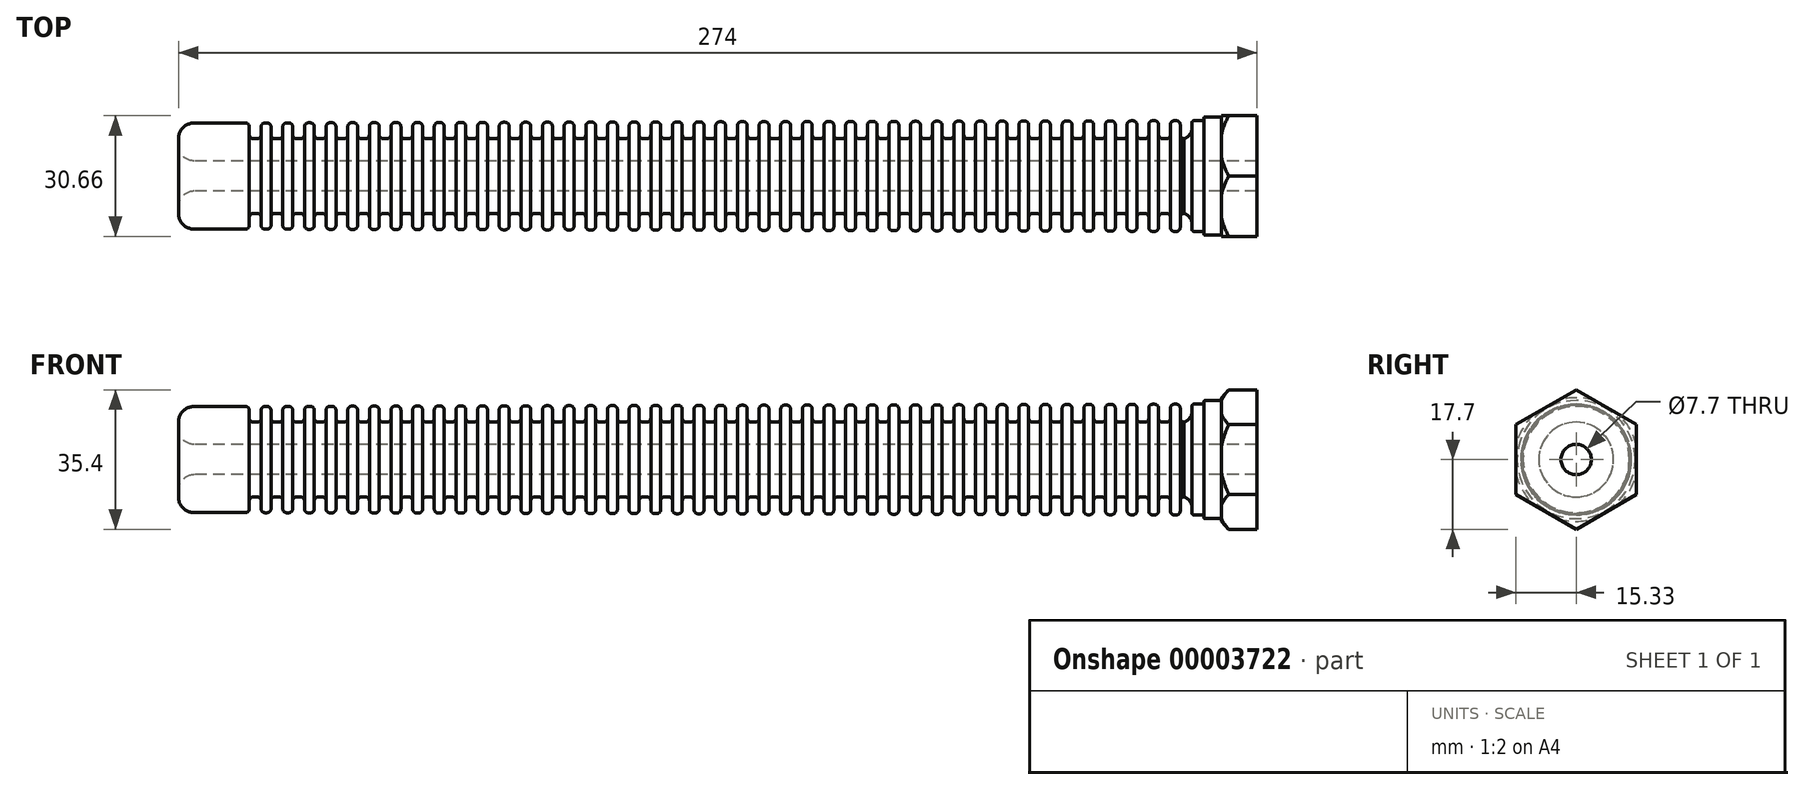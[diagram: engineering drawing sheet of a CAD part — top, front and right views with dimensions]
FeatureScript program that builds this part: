
annotation { "Feature Type Name" : "Feature", "Feature Type Description" : "" }
export const myFeature = defineFeature(function(context is Context, id is Id, definition is map)
    precondition{}
    {
        {
            var Q0;
            Q0=qCreatedBy(makeId("Front.planeOp"),FACE);
            var sketch = newSketch(context, id + "F0", { "sketchPlane" : qUnion([Q0])});
            skLineSegment(sketch, "E0", {"start": v(-577.5, 0) * mm, "end": v(0, 0) * mm, "construction": true});
            skLineSegment(sketch, "E1.0.MirrorCS", {"start": v(577.5, 0) * mm, "end": v(0, 0) * mm, "construction": true});
            skLineSegment(sketch, "E2", {"start": v(-577.5, 0) * mm, "end": v(-577.5, 13.5) * mm, "construction": true});
            skLineSegment(sketch, "E3.0.MirrorCS", {"start": v(-577.5, 0) * mm, "end": v(-577.5, -13.5) * mm, "construction": true});
            skLineSegment(sketch, "E4", {"start": v(-577.5, 13.5) * mm, "end": v(-577.5, 3.85) * mm});
            skLineSegment(sketch, "E5.0.MirrorCS", {"start": v(-577.5, -13.5) * mm, "end": v(-577.5, -3.85) * mm});
            skLineSegment(sketch, "E6", {"start": v(-577.5, 3.85) * mm, "end": v(-559.5, 3.85) * mm});
            skLineSegment(sketch, "E7", {"start": v(-577.5, 13.5) * mm, "end": v(-559.5, 13.5) * mm});
            skLineSegment(sketch, "E8.0.MirrorCS", {"start": v(-577.5, -13.5) * mm, "end": v(-559.5, -13.5) * mm});
            skLineSegment(sketch, "E9.0.MirrorCS", {"start": v(-577.5, -3.85) * mm, "end": v(56.5, -3.85) * mm});
            skLineSegment(sketch, "E10", {"start": v(-559.5, 13.5) * mm, "end": v(-559.5, 3.85) * mm});
            skPoint(sketch, "E11", {"position": v(-577.5, 15) * mm});
            skPoint(sketch, "E12.0.MirrorP", {"position": v(-577.5, -15) * mm});
            skLineSegment(sketch, "E13", {"start": v(-577.5, 15) * mm, "end": v(56.5, 15) * mm, "construction": true});
            skLineSegment(sketch, "E14", {"start": v(-559.5, 9.5) * mm, "end": v(-559.5, 9.5) * mm});
            skPoint(sketch, "E15.trimOffspring.end.orphan", {"position": v(56.5, 3.85) * mm});
            skLineSegment(sketch, "E16", {"start": v(-559.5, 3.85) * mm, "end": v(56.5, 3.85) * mm});
            skPoint(sketch, "E17.end.orphan", {"position": v(-559.5, 13.5) * mm});
            skLineSegment(sketch, "E18", {"start": v(-559.5, 13.5) * mm, "end": v(-559.5, 13.5) * mm});
            skLineSegment(sketch, "E19", {"start": v(-559.5, 13.5) * mm, "end": v(56.5, 15) * mm, "construction": true});
            skLineSegment(sketch, "E20", {"start": v(-559.5, 9.5) * mm, "end": v(56.5, 9.5) * mm});
            skLineSegment(sketch, "E21", {"start": v(-559.5, 13.5) * mm, "end": v(56.5, 13.5) * mm, "construction": true});
            skLineSegment(sketch, "E22", {"start": v(-556.5, 13.5) * mm, "end": v(-556.5, 9.5) * mm});
            skLineSegment(sketch, "E23", {"start": v(-556.5, 13.5) * mm, "end": v(-554, 13.5) * mm});
            skLineSegment(sketch, "E24", {"start": v(-554, 13.5) * mm, "end": v(-554, 9.5) * mm});
            skLineSegment(sketch, "E25", {"start": v(-551, 13.52) * mm, "end": v(-551, 13.5) * mm});
            skLineSegment(sketch, "E26", {"start": v(-551, 13.52) * mm, "end": v(-548.5, 13.52) * mm});
            skLineSegment(sketch, "E27", {"start": v(-548.5, 13.52) * mm, "end": v(-548.5, 9.5) * mm});
            skPoint(sketch, "E28", {"position": v(-312.5, 3.85) * mm});
            skLineSegment(sketch, "E29", {"start": v(-545.5, 13.53) * mm, "end": v(-545.5, 9.5) * mm});
            skLineSegment(sketch, "E30", {"start": v(-545.5, 13.53) * mm, "end": v(-543, 13.53) * mm});
            skLineSegment(sketch, "E31", {"start": v(-543, 13.53) * mm, "end": v(-543, 9.5) * mm});
            skLineSegment(sketch, "E32", {"start": v(-540, 13.55) * mm, "end": v(-540, 9.5) * mm});
            skLineSegment(sketch, "E33", {"start": v(-540, 13.55) * mm, "end": v(-537.5, 13.55) * mm});
            skLineSegment(sketch, "E34", {"start": v(-537.5, 13.55) * mm, "end": v(-537.5, 9.5) * mm});
            skLineSegment(sketch, "E35", {"start": v(-534.5, 13.56) * mm, "end": v(-534.5, 9.5) * mm});
            skLineSegment(sketch, "E36", {"start": v(-534.5, 13.56) * mm, "end": v(-532, 13.56) * mm});
            skLineSegment(sketch, "E37", {"start": v(-532, 13.56) * mm, "end": v(-532, 9.5) * mm});
            skLineSegment(sketch, "E38", {"start": v(-529, 13.57) * mm, "end": v(-529, 9.5) * mm});
            skLineSegment(sketch, "E39", {"start": v(-529, 13.57) * mm, "end": v(-526.5, 13.57) * mm});
            skLineSegment(sketch, "E40", {"start": v(-526.5, 13.57) * mm, "end": v(-526.5, 9.5) * mm});
            skLineSegment(sketch, "E41", {"start": v(-523.5, 13.59) * mm, "end": v(-523.5, 9.5) * mm});
            skLineSegment(sketch, "E42", {"start": v(-523.5, 13.59) * mm, "end": v(-521, 13.59) * mm});
            skLineSegment(sketch, "E43", {"start": v(-521, 13.59) * mm, "end": v(-521, 9.5) * mm});
            skLineSegment(sketch, "E44", {"start": v(-518, 13.6) * mm, "end": v(-518, 9.5) * mm});
            skLineSegment(sketch, "E45", {"start": v(-518, 13.6) * mm, "end": v(-515.5, 13.6) * mm});
            skLineSegment(sketch, "E46", {"start": v(-515.5, 13.6) * mm, "end": v(-515.5, 9.5) * mm});
            skLineSegment(sketch, "E47", {"start": v(-512.5, 13.61) * mm, "end": v(-512.5, 9.5) * mm});
            skLineSegment(sketch, "E48", {"start": v(-512.5, 13.61) * mm, "end": v(-510, 13.61) * mm});
            skLineSegment(sketch, "E49", {"start": v(-510, 13.61) * mm, "end": v(-510, 9.5) * mm});
            skLineSegment(sketch, "E50", {"start": v(-551, 13.5) * mm, "end": v(-551, 9.5) * mm});
            skLineSegment(sketch, "E51", {"start": v(-507, 13.63) * mm, "end": v(-507, 9.5) * mm});
            skLineSegment(sketch, "E52", {"start": v(-507, 13.63) * mm, "end": v(-504.5, 13.63) * mm});
            skLineSegment(sketch, "E53", {"start": v(-504.5, 13.63) * mm, "end": v(-504.5, 9.5) * mm});
            skLineSegment(sketch, "E54", {"start": v(-501.5, 13.64) * mm, "end": v(-501.5, 9.5) * mm});
            skLineSegment(sketch, "E55", {"start": v(-501.5, 13.64) * mm, "end": v(-499, 13.64) * mm});
            skLineSegment(sketch, "E56", {"start": v(-499, 13.64) * mm, "end": v(-499, 9.5) * mm});
            skLineSegment(sketch, "E57", {"start": v(-496, 13.65) * mm, "end": v(-496, 9.5) * mm});
            skLineSegment(sketch, "E58", {"start": v(-496, 13.65) * mm, "end": v(-493.5, 13.65) * mm});
            skLineSegment(sketch, "E59", {"start": v(-493.5, 13.65) * mm, "end": v(-493.5, 9.5) * mm});
            skLineSegment(sketch, "E60", {"start": v(-490.5, 13.67) * mm, "end": v(-490.5, 9.5) * mm});
            skLineSegment(sketch, "E61", {"start": v(-490.5, 13.67) * mm, "end": v(-488, 13.67) * mm});
            skLineSegment(sketch, "E62", {"start": v(-488, 13.67) * mm, "end": v(-488, 9.5) * mm});
            skLineSegment(sketch, "E63", {"start": v(-485, 13.68) * mm, "end": v(-485, 9.5) * mm});
            skLineSegment(sketch, "E64", {"start": v(-485, 13.68) * mm, "end": v(-482.5, 13.68) * mm});
            skLineSegment(sketch, "E65", {"start": v(-482.5, 13.68) * mm, "end": v(-482.5, 9.5) * mm});
            skLineSegment(sketch, "E66", {"start": v(-479.5, 13.7) * mm, "end": v(-479.5, 9.5) * mm});
            skLineSegment(sketch, "E67", {"start": v(-479.5, 13.7) * mm, "end": v(-477, 13.7) * mm});
            skLineSegment(sketch, "E68", {"start": v(-477, 13.7) * mm, "end": v(-477, 9.5) * mm});
            skLineSegment(sketch, "E69", {"start": v(-474, 13.7) * mm, "end": v(-474, 9.5) * mm});
            skLineSegment(sketch, "E70", {"start": v(-474, 13.7) * mm, "end": v(-471.5, 13.7) * mm});
            skLineSegment(sketch, "E71", {"start": v(-471.5, 13.7) * mm, "end": v(-471.5, 9.5) * mm});
            skLineSegment(sketch, "E72", {"start": v(-468.5, 13.72) * mm, "end": v(-468.5, 9.5) * mm});
            skLineSegment(sketch, "E73", {"start": v(-468.5, 13.72) * mm, "end": v(-466, 13.72) * mm});
            skLineSegment(sketch, "E74", {"start": v(-466, 13.72) * mm, "end": v(-466, 9.5) * mm});
            skLineSegment(sketch, "E75", {"start": v(-463, 13.73) * mm, "end": v(-463, 9.5) * mm});
            skLineSegment(sketch, "E76", {"start": v(-463, 13.73) * mm, "end": v(-460.5, 13.73) * mm});
            skLineSegment(sketch, "E77", {"start": v(-460.5, 13.73) * mm, "end": v(-460.5, 9.5) * mm});
            skLineSegment(sketch, "E78", {"start": v(-457.5, 13.75) * mm, "end": v(-457.5, 9.5) * mm});
            skLineSegment(sketch, "E79", {"start": v(-457.5, 13.75) * mm, "end": v(-455, 13.75) * mm});
            skLineSegment(sketch, "E80", {"start": v(-455, 13.75) * mm, "end": v(-455, 9.5) * mm});
            skLineSegment(sketch, "E81", {"start": v(-312.5, 50.5) * mm, "end": v(-312.5, -48.82) * mm, "construction": true});
            skLineSegment(sketch, "E82", {"start": v(-452, 13.76) * mm, "end": v(-452, 9.5) * mm});
            skLineSegment(sketch, "E83", {"start": v(-452, 13.76) * mm, "end": v(-449.5, 13.76) * mm});
            skLineSegment(sketch, "E84", {"start": v(-449.5, 13.76) * mm, "end": v(-449.5, 9.5) * mm});
            skLineSegment(sketch, "E85", {"start": v(-446.5, 9.5) * mm, "end": v(-446.5, 13.78) * mm});
            skLineSegment(sketch, "E86", {"start": v(-446.5, 13.78) * mm, "end": v(-444, 13.78) * mm});
            skLineSegment(sketch, "E87", {"start": v(-444, 13.78) * mm, "end": v(-444, 9.5) * mm});
            skLineSegment(sketch, "E88", {"start": v(-441, 13.79) * mm, "end": v(-441, 9.5) * mm});
            skLineSegment(sketch, "E89", {"start": v(-441, 13.79) * mm, "end": v(-438.5, 13.79) * mm});
            skLineSegment(sketch, "E90", {"start": v(-438.5, 13.79) * mm, "end": v(-438.5, 9.5) * mm});
            skLineSegment(sketch, "E91", {"start": v(-435.5, 13.8) * mm, "end": v(-435.5, 9.5) * mm});
            skLineSegment(sketch, "E92", {"start": v(-435.5, 13.8) * mm, "end": v(-433, 13.8) * mm});
            skLineSegment(sketch, "E93", {"start": v(-433, 13.8) * mm, "end": v(-433, 9.5) * mm});
            skLineSegment(sketch, "E94", {"start": v(-430, 13.82) * mm, "end": v(-430, 9.5) * mm});
            skLineSegment(sketch, "E95", {"start": v(-430, 13.82) * mm, "end": v(-427.5, 13.82) * mm});
            skLineSegment(sketch, "E96", {"start": v(-427.5, 13.82) * mm, "end": v(-427.5, 9.5) * mm});
            skLineSegment(sketch, "E97", {"start": v(-424.5, 9.5) * mm, "end": v(-424.5, 13.83) * mm});
            skLineSegment(sketch, "E98", {"start": v(-424.5, 13.83) * mm, "end": v(-422, 13.83) * mm});
            skLineSegment(sketch, "E99", {"start": v(-422, 13.83) * mm, "end": v(-422, 9.5) * mm});
            skLineSegment(sketch, "E100", {"start": v(-419, 13.84) * mm, "end": v(-419, 9.5) * mm});
            skLineSegment(sketch, "E101", {"start": v(-419, 13.84) * mm, "end": v(-416.5, 13.84) * mm});
            skLineSegment(sketch, "E102", {"start": v(-416.5, 13.84) * mm, "end": v(-416.5, 9.5) * mm});
            skLineSegment(sketch, "E103", {"start": v(-413.5, 13.86) * mm, "end": v(-413.5, 9.5) * mm});
            skLineSegment(sketch, "E104", {"start": v(-413.5, 13.86) * mm, "end": v(-411, 13.86) * mm});
            skLineSegment(sketch, "E105", {"start": v(-411, 13.86) * mm, "end": v(-411, 9.5) * mm});
            skLineSegment(sketch, "E106", {"start": v(-408, 9.5) * mm, "end": v(-408, 13.87) * mm});
            skLineSegment(sketch, "E107", {"start": v(-408, 13.87) * mm, "end": v(-405.5, 13.87) * mm});
            skLineSegment(sketch, "E108", {"start": v(-405.5, 13.87) * mm, "end": v(-405.5, 9.5) * mm});
            skLineSegment(sketch, "E109", {"start": v(-402.5, 9.5) * mm, "end": v(-402.5, 13.88) * mm});
            skLineSegment(sketch, "E110", {"start": v(-402.5, 13.88) * mm, "end": v(-400, 13.88) * mm});
            skLineSegment(sketch, "E111", {"start": v(-400, 13.88) * mm, "end": v(-400, 9.5) * mm});
            skLineSegment(sketch, "E112", {"start": v(-397, 9.5) * mm, "end": v(-397, 13.9) * mm});
            skLineSegment(sketch, "E113", {"start": v(-397, 13.9) * mm, "end": v(-394.5, 13.9) * mm});
            skLineSegment(sketch, "E114", {"start": v(-394.5, 13.9) * mm, "end": v(-394.5, 9.5) * mm});
            skLineSegment(sketch, "E115", {"start": v(-391.5, 9.5) * mm, "end": v(-391.5, 13.9) * mm});
            skLineSegment(sketch, "E116", {"start": v(-391.5, 13.9) * mm, "end": v(-389, 13.9) * mm});
            skLineSegment(sketch, "E117", {"start": v(-389, 13.9) * mm, "end": v(-389, 9.5) * mm});
            skLineSegment(sketch, "E118", {"start": v(-386, 9.5) * mm, "end": v(-386, 13.92) * mm});
            skLineSegment(sketch, "E119", {"start": v(-386, 13.92) * mm, "end": v(-383.5, 13.92) * mm});
            skLineSegment(sketch, "E120", {"start": v(-383.5, 13.92) * mm, "end": v(-383.5, 9.5) * mm});
            skLineSegment(sketch, "E121", {"start": v(-380.49, 9.5) * mm, "end": v(-380.5, 13.94) * mm});
            skLineSegment(sketch, "E122", {"start": v(-380.5, 13.94) * mm, "end": v(-378, 13.94) * mm});
            skLineSegment(sketch, "E123", {"start": v(-378, 13.94) * mm, "end": v(-378, 9.5) * mm});
            skLineSegment(sketch, "E124", {"start": v(-375, 9.5) * mm, "end": v(-375, 13.95) * mm});
            skLineSegment(sketch, "E125", {"start": v(-375, 13.95) * mm, "end": v(-372.5, 13.95) * mm});
            skLineSegment(sketch, "E126", {"start": v(-372.5, 13.95) * mm, "end": v(-372.5, 9.5) * mm});
            skLineSegment(sketch, "E127", {"start": v(-369.5, 9.5) * mm, "end": v(-369.5, 13.96) * mm});
            skLineSegment(sketch, "E128", {"start": v(-369.5, 13.96) * mm, "end": v(-367, 13.96) * mm});
            skLineSegment(sketch, "E129", {"start": v(-367, 13.96) * mm, "end": v(-367, 9.5) * mm});
            skLineSegment(sketch, "E130", {"start": v(-364, 9.5) * mm, "end": v(-364, 13.98) * mm});
            skLineSegment(sketch, "E131", {"start": v(-364, 13.98) * mm, "end": v(-361.5, 13.98) * mm});
            skLineSegment(sketch, "E132", {"start": v(-361.5, 13.98) * mm, "end": v(-361.5, 9.5) * mm});
            skLineSegment(sketch, "E133", {"start": v(-358.49, 9.5) * mm, "end": v(-358.5, 13.99) * mm});
            skLineSegment(sketch, "E134", {"start": v(-358.5, 13.99) * mm, "end": v(-356, 13.99) * mm});
            skLineSegment(sketch, "E135", {"start": v(-356, 13.99) * mm, "end": v(-355.99, 9.5) * mm});
            skLineSegment(sketch, "E136", {"start": v(-353, 9.5) * mm, "end": v(-353, 14) * mm});
            skLineSegment(sketch, "E137", {"start": v(-353, 14) * mm, "end": v(-350.5, 14) * mm});
            skLineSegment(sketch, "E138", {"start": v(-350.5, 14) * mm, "end": v(-350.5, 9.5) * mm});
            skLineSegment(sketch, "E139", {"start": v(-347.5, 9.5) * mm, "end": v(-347.5, 14.02) * mm});
            skLineSegment(sketch, "E140", {"start": v(-347.5, 14.02) * mm, "end": v(-345, 14.02) * mm});
            skLineSegment(sketch, "E141", {"start": v(-345, 14.02) * mm, "end": v(-345, 9.5) * mm});
            skLineSegment(sketch, "E142", {"start": v(-342, 9.5) * mm, "end": v(-342, 14.03) * mm});
            skLineSegment(sketch, "E143", {"start": v(-342, 14.03) * mm, "end": v(-339.5, 14.03) * mm});
            skLineSegment(sketch, "E144", {"start": v(-339.5, 14.03) * mm, "end": v(-339.5, 9.5) * mm});
            skLineSegment(sketch, "E145", {"start": v(-336.5, 9.5) * mm, "end": v(-336.5, 14.04) * mm});
            skLineSegment(sketch, "E146", {"start": v(-336.5, 14.04) * mm, "end": v(-334, 14.04) * mm});
            skLineSegment(sketch, "E147", {"start": v(-334, 14.04) * mm, "end": v(-334, 9.5) * mm});
            skLineSegment(sketch, "E148", {"start": v(-330.99, 9.5) * mm, "end": v(-331, 14.06) * mm});
            skLineSegment(sketch, "E149", {"start": v(-331, 14.06) * mm, "end": v(-328.5, 14.06) * mm});
            skLineSegment(sketch, "E150", {"start": v(-328.5, 14.06) * mm, "end": v(-328.5, 9.5) * mm});
            skLineSegment(sketch, "E151", {"start": v(-325.5, 9.5) * mm, "end": v(-325.5, 14.07) * mm});
            skLineSegment(sketch, "E152", {"start": v(-325.5, 14.07) * mm, "end": v(-323, 14.07) * mm});
            skLineSegment(sketch, "E153", {"start": v(-323, 14.07) * mm, "end": v(-323, 9.5) * mm});
            skLineSegment(sketch, "E154", {"start": v(-320, 9.5) * mm, "end": v(-320, 14.08) * mm});
            skLineSegment(sketch, "E155", {"start": v(-320, 14.08) * mm, "end": v(-317, 14.08) * mm});
            skLineSegment(sketch, "E156", {"start": v(-317, 14.08) * mm, "end": v(-317, 9.5) * mm});
            skLineSegment(sketch, "E157", {"start": v(-317, 14.08) * mm, "end": v(-317, 15) * mm});
            skLineSegment(sketch, "E158", {"start": v(-317, 15) * mm, "end": v(-312.5, 15) * mm});
            skLineSegment(sketch, "E159", {"start": v(-312.5, 15) * mm, "end": v(-312.5, 9.5) * mm});
            skLineSegment(sketch, "E160", {"start": v(-312.5, 9.5) * mm, "end": v(-312.5, 3.85) * mm});
            skSolve(sketch);
        }
        {
            var Q0;
            Q0 = qSketchRegion(id + "F0", true);
            var Q1;
            Q1=sQuery(id+"F0.wireOp",EDGE,"E0");
            revolve(context, id + "F1", {"entities" : qUnion([Q0]), "axis" : qUnion([Q1]), "revolveType" : RevolveType.FULL});
        }
        {
            var Q0;
            Q0=makeQuery(id+"F1.opRevolve","SWEPT_EDGE",EDGE,{"disambiguationData":[OSD([sQuery(id+"F0.wireOp",EDGE,"E4"),sQuery(id+"F0.wireOp",EDGE,"E7")])]});
            var Q1;
            Q1=makeQuery(id+"F1.opRevolve","SWEPT_EDGE",EDGE,{"disambiguationData":[OSD([sQuery(id+"F0.wireOp",EDGE,"E4"),sQuery(id+"F0.wireOp",EDGE,"E6")])]});
            fillet(context, id + "F2", {"entities" : qUnion([Q0, Q1]), "radius" : 4 * mm, "tangentPropagation" : true, "allowEdgeOverflow" : false});
        }
        {
            var Q0;
            Q0=makeQuery(id+"F1.opRevolve","SWEPT_EDGE",EDGE,{"disambiguationData":[OSD([sQuery(id+"F0.wireOp",EDGE,"E7"),sQuery(id+"F0.wireOp",EDGE,"E10")])]});
            var Q1;
            {var subQ0=sQuery(id+"F0.wireOp",EDGE,"E20");Q1=makeQuery(id+"F1.opRevolve","SWEPT_FACE",FACE,{"disambiguationData":[OSD([subQ0]),TDD([makeQuery(id+"F0.imprint","IMPRINT",EDGE,{"disambiguationData":[TD([[makeQuery(id+"F0.imprint","INTERSECT",VERTEX,{"derivedFrom":[sQuery(id+"F0.wireOp",EDGE,"E10"),subQ0]}),-1.0]])],"derivedFrom":subQ0})])]});}
            var Q2;
            Q2=makeQuery(id+"F1.opRevolve","SWEPT_FACE",FACE,{"disambiguationData":[OSD([sQuery(id+"F0.wireOp",EDGE,"E23")])]});
            var Q3;
            {var subQ0=sQuery(id+"F0.wireOp",EDGE,"E20");Q3=makeQuery(id+"F1.opRevolve","SWEPT_FACE",FACE,{"disambiguationData":[OSD([subQ0]),TDD([makeQuery(id+"F0.imprint","IMPRINT",EDGE,{"disambiguationData":[TD([[makeQuery(id+"F0.imprint","INTERSECT",VERTEX,{"derivedFrom":[subQ0,sQuery(id+"F0.wireOp",EDGE,"E24")]}),-1.0]])],"derivedFrom":subQ0})])]});}
            var Q4;
            Q4=makeQuery(id+"F1.opRevolve","SWEPT_FACE",FACE,{"disambiguationData":[OSD([sQuery(id+"F0.wireOp",EDGE,"E26")])]});
            var Q5;
            {var subQ0=sQuery(id+"F0.wireOp",EDGE,"E20");Q5=makeQuery(id+"F1.opRevolve","SWEPT_FACE",FACE,{"disambiguationData":[OSD([subQ0]),TDD([makeQuery(id+"F0.imprint","IMPRINT",EDGE,{"disambiguationData":[TD([[makeQuery(id+"F0.imprint","INTERSECT",VERTEX,{"derivedFrom":[subQ0,sQuery(id+"F0.wireOp",EDGE,"E27")]}),-1.0]])],"derivedFrom":subQ0})])]});}
            var Q6;
            Q6=makeQuery(id+"F1.opRevolve","SWEPT_FACE",FACE,{"disambiguationData":[OSD([sQuery(id+"F0.wireOp",EDGE,"E30")])]});
            var Q7;
            {var subQ0=sQuery(id+"F0.wireOp",EDGE,"E20");Q7=makeQuery(id+"F1.opRevolve","SWEPT_FACE",FACE,{"disambiguationData":[OSD([subQ0]),TDD([makeQuery(id+"F0.imprint","IMPRINT",EDGE,{"disambiguationData":[TD([[makeQuery(id+"F0.imprint","INTERSECT",VERTEX,{"derivedFrom":[subQ0,sQuery(id+"F0.wireOp",EDGE,"E31")]}),-1.0]])],"derivedFrom":subQ0})])]});}
            var Q8;
            Q8=makeQuery(id+"F1.opRevolve","SWEPT_FACE",FACE,{"disambiguationData":[OSD([sQuery(id+"F0.wireOp",EDGE,"E33")])]});
            var Q9;
            {var subQ0=sQuery(id+"F0.wireOp",EDGE,"E20");Q9=makeQuery(id+"F1.opRevolve","SWEPT_FACE",FACE,{"disambiguationData":[OSD([subQ0]),TDD([makeQuery(id+"F0.imprint","IMPRINT",EDGE,{"disambiguationData":[TD([[makeQuery(id+"F0.imprint","INTERSECT",VERTEX,{"derivedFrom":[subQ0,sQuery(id+"F0.wireOp",EDGE,"E34")]}),-1.0]])],"derivedFrom":subQ0})])]});}
            var Q10;
            {var subQ0=sQuery(id+"F0.wireOp",EDGE,"E20");Q10=makeQuery(id+"F1.opRevolve","SWEPT_FACE",FACE,{"disambiguationData":[OSD([subQ0]),TDD([makeQuery(id+"F0.imprint","IMPRINT",EDGE,{"disambiguationData":[TD([[makeQuery(id+"F0.imprint","INTERSECT",VERTEX,{"derivedFrom":[subQ0,sQuery(id+"F0.wireOp",EDGE,"E37")]}),-1.0]])],"derivedFrom":subQ0})])]});}
            var Q11;
            Q11=makeQuery(id+"F1.opRevolve","SWEPT_FACE",FACE,{"disambiguationData":[OSD([sQuery(id+"F0.wireOp",EDGE,"E39")])]});
            var Q12;
            {var subQ0=sQuery(id+"F0.wireOp",EDGE,"E20");Q12=makeQuery(id+"F1.opRevolve","SWEPT_FACE",FACE,{"disambiguationData":[OSD([subQ0]),TDD([makeQuery(id+"F0.imprint","IMPRINT",EDGE,{"disambiguationData":[TD([[makeQuery(id+"F0.imprint","INTERSECT",VERTEX,{"derivedFrom":[subQ0,sQuery(id+"F0.wireOp",EDGE,"E40")]}),-1.0]])],"derivedFrom":subQ0})])]});}
            var Q13;
            Q13=makeQuery(id+"F1.opRevolve","SWEPT_FACE",FACE,{"disambiguationData":[OSD([sQuery(id+"F0.wireOp",EDGE,"E42")])]});
            var Q14;
            {var subQ0=sQuery(id+"F0.wireOp",EDGE,"E20");Q14=makeQuery(id+"F1.opRevolve","SWEPT_FACE",FACE,{"disambiguationData":[OSD([subQ0]),TDD([makeQuery(id+"F0.imprint","IMPRINT",EDGE,{"disambiguationData":[TD([[makeQuery(id+"F0.imprint","INTERSECT",VERTEX,{"derivedFrom":[subQ0,sQuery(id+"F0.wireOp",EDGE,"E43")]}),-1.0]])],"derivedFrom":subQ0})])]});}
            var Q15;
            Q15=makeQuery(id+"F1.opRevolve","SWEPT_FACE",FACE,{"disambiguationData":[OSD([sQuery(id+"F0.wireOp",EDGE,"E45")])]});
            var Q16;
            {var subQ0=sQuery(id+"F0.wireOp",EDGE,"E20");Q16=makeQuery(id+"F1.opRevolve","SWEPT_FACE",FACE,{"disambiguationData":[OSD([subQ0]),TDD([makeQuery(id+"F0.imprint","IMPRINT",EDGE,{"disambiguationData":[TD([[makeQuery(id+"F0.imprint","INTERSECT",VERTEX,{"derivedFrom":[subQ0,sQuery(id+"F0.wireOp",EDGE,"E46")]}),-1.0]])],"derivedFrom":subQ0})])]});}
            var Q17;
            Q17=makeQuery(id+"F1.opRevolve","SWEPT_FACE",FACE,{"disambiguationData":[OSD([sQuery(id+"F0.wireOp",EDGE,"E36")])]});
            var Q18;
            Q18=makeQuery(id+"F1.opRevolve","SWEPT_FACE",FACE,{"disambiguationData":[OSD([sQuery(id+"F0.wireOp",EDGE,"E48")])]});
            var Q19;
            {var subQ0=sQuery(id+"F0.wireOp",EDGE,"E20");Q19=makeQuery(id+"F1.opRevolve","SWEPT_FACE",FACE,{"disambiguationData":[OSD([subQ0]),TDD([makeQuery(id+"F0.imprint","IMPRINT",EDGE,{"disambiguationData":[TD([[makeQuery(id+"F0.imprint","INTERSECT",VERTEX,{"derivedFrom":[subQ0,sQuery(id+"F0.wireOp",EDGE,"E49")]}),-1.0]])],"derivedFrom":subQ0})])]});}
            var Q20;
            Q20=makeQuery(id+"F1.opRevolve","SWEPT_FACE",FACE,{"disambiguationData":[OSD([sQuery(id+"F0.wireOp",EDGE,"E52")])]});
            var Q21;
            {var subQ0=sQuery(id+"F0.wireOp",EDGE,"E20");Q21=makeQuery(id+"F1.opRevolve","SWEPT_FACE",FACE,{"disambiguationData":[OSD([subQ0]),TDD([makeQuery(id+"F0.imprint","IMPRINT",EDGE,{"disambiguationData":[TD([[makeQuery(id+"F0.imprint","INTERSECT",VERTEX,{"derivedFrom":[subQ0,sQuery(id+"F0.wireOp",EDGE,"E53")]}),-1.0]])],"derivedFrom":subQ0})])]});}
            var Q22;
            {var subQ0=sQuery(id+"F0.wireOp",EDGE,"E20");Q22=makeQuery(id+"F1.opRevolve","SWEPT_FACE",FACE,{"disambiguationData":[OSD([subQ0]),TDD([makeQuery(id+"F0.imprint","IMPRINT",EDGE,{"disambiguationData":[TD([[makeQuery(id+"F0.imprint","INTERSECT",VERTEX,{"derivedFrom":[subQ0,sQuery(id+"F0.wireOp",EDGE,"E56")]}),-1.0]])],"derivedFrom":subQ0})])]});}
            var Q23;
            Q23=makeQuery(id+"F1.opRevolve","SWEPT_FACE",FACE,{"disambiguationData":[OSD([sQuery(id+"F0.wireOp",EDGE,"E55")])]});
            var Q24;
            Q24=makeQuery(id+"F1.opRevolve","SWEPT_FACE",FACE,{"disambiguationData":[OSD([sQuery(id+"F0.wireOp",EDGE,"E52")])]});
            var Q25;
            Q25=makeQuery(id+"F1.opRevolve","SWEPT_FACE",FACE,{"disambiguationData":[OSD([sQuery(id+"F0.wireOp",EDGE,"E58")])]});
            var Q26;
            {var subQ0=sQuery(id+"F0.wireOp",EDGE,"E20");Q26=makeQuery(id+"F1.opRevolve","SWEPT_FACE",FACE,{"disambiguationData":[OSD([subQ0]),TDD([makeQuery(id+"F0.imprint","IMPRINT",EDGE,{"disambiguationData":[TD([[makeQuery(id+"F0.imprint","INTERSECT",VERTEX,{"derivedFrom":[subQ0,sQuery(id+"F0.wireOp",EDGE,"E59")]}),-1.0]])],"derivedFrom":subQ0})])]});}
            var Q27;
            Q27=makeQuery(id+"F1.opRevolve","SWEPT_FACE",FACE,{"disambiguationData":[OSD([sQuery(id+"F0.wireOp",EDGE,"E61")])]});
            var Q28;
            {var subQ0=sQuery(id+"F0.wireOp",EDGE,"E20");Q28=makeQuery(id+"F1.opRevolve","SWEPT_FACE",FACE,{"disambiguationData":[OSD([subQ0]),TDD([makeQuery(id+"F0.imprint","IMPRINT",EDGE,{"disambiguationData":[TD([[makeQuery(id+"F0.imprint","INTERSECT",VERTEX,{"derivedFrom":[subQ0,sQuery(id+"F0.wireOp",EDGE,"E62")]}),-1.0]])],"derivedFrom":subQ0})])]});}
            var Q29;
            Q29=makeQuery(id+"F1.opRevolve","SWEPT_FACE",FACE,{"disambiguationData":[OSD([sQuery(id+"F0.wireOp",EDGE,"E64")])]});
            var Q30;
            {var subQ0=sQuery(id+"F0.wireOp",EDGE,"E20");Q30=makeQuery(id+"F1.opRevolve","SWEPT_FACE",FACE,{"disambiguationData":[OSD([subQ0]),TDD([makeQuery(id+"F0.imprint","IMPRINT",EDGE,{"disambiguationData":[TD([[makeQuery(id+"F0.imprint","INTERSECT",VERTEX,{"derivedFrom":[subQ0,sQuery(id+"F0.wireOp",EDGE,"E65")]}),-1.0]])],"derivedFrom":subQ0})])]});}
            var Q31;
            Q31=makeQuery(id+"F1.opRevolve","SWEPT_FACE",FACE,{"disambiguationData":[OSD([sQuery(id+"F0.wireOp",EDGE,"E67")])]});
            var Q32;
            {var subQ0=sQuery(id+"F0.wireOp",EDGE,"E20");Q32=makeQuery(id+"F1.opRevolve","SWEPT_FACE",FACE,{"disambiguationData":[OSD([subQ0]),TDD([makeQuery(id+"F0.imprint","IMPRINT",EDGE,{"disambiguationData":[TD([[makeQuery(id+"F0.imprint","INTERSECT",VERTEX,{"derivedFrom":[subQ0,sQuery(id+"F0.wireOp",EDGE,"E68")]}),-1.0]])],"derivedFrom":subQ0})])]});}
            var Q33;
            Q33=makeQuery(id+"F1.opRevolve","SWEPT_FACE",FACE,{"disambiguationData":[OSD([sQuery(id+"F0.wireOp",EDGE,"E70")])]});
            var Q34;
            {var subQ0=sQuery(id+"F0.wireOp",EDGE,"E20");Q34=makeQuery(id+"F1.opRevolve","SWEPT_FACE",FACE,{"disambiguationData":[OSD([subQ0]),TDD([makeQuery(id+"F0.imprint","IMPRINT",EDGE,{"disambiguationData":[TD([[makeQuery(id+"F0.imprint","INTERSECT",VERTEX,{"derivedFrom":[subQ0,sQuery(id+"F0.wireOp",EDGE,"E71")]}),-1.0]])],"derivedFrom":subQ0})])]});}
            var Q35;
            Q35=makeQuery(id+"F1.opRevolve","SWEPT_FACE",FACE,{"disambiguationData":[OSD([sQuery(id+"F0.wireOp",EDGE,"E73")])]});
            var Q36;
            {var subQ0=sQuery(id+"F0.wireOp",EDGE,"E20");Q36=makeQuery(id+"F1.opRevolve","SWEPT_FACE",FACE,{"disambiguationData":[OSD([subQ0]),TDD([makeQuery(id+"F0.imprint","IMPRINT",EDGE,{"disambiguationData":[TD([[makeQuery(id+"F0.imprint","INTERSECT",VERTEX,{"derivedFrom":[subQ0,sQuery(id+"F0.wireOp",EDGE,"E74")]}),-1.0]])],"derivedFrom":subQ0})])]});}
            var Q37;
            Q37=makeQuery(id+"F1.opRevolve","SWEPT_FACE",FACE,{"disambiguationData":[OSD([sQuery(id+"F0.wireOp",EDGE,"E76")])]});
            var Q38;
            {var subQ0=sQuery(id+"F0.wireOp",EDGE,"E20");Q38=makeQuery(id+"F1.opRevolve","SWEPT_FACE",FACE,{"disambiguationData":[OSD([subQ0]),TDD([makeQuery(id+"F0.imprint","IMPRINT",EDGE,{"disambiguationData":[TD([[makeQuery(id+"F0.imprint","INTERSECT",VERTEX,{"derivedFrom":[subQ0,sQuery(id+"F0.wireOp",EDGE,"E77")]}),-1.0]])],"derivedFrom":subQ0})])]});}
            var Q39;
            Q39=makeQuery(id+"F1.opRevolve","SWEPT_FACE",FACE,{"disambiguationData":[OSD([sQuery(id+"F0.wireOp",EDGE,"E79")])]});
            var Q40;
            {var subQ0=sQuery(id+"F0.wireOp",EDGE,"E20");Q40=makeQuery(id+"F1.opRevolve","SWEPT_FACE",FACE,{"disambiguationData":[OSD([subQ0]),TDD([makeQuery(id+"F0.imprint","IMPRINT",EDGE,{"disambiguationData":[TD([[makeQuery(id+"F0.imprint","INTERSECT",VERTEX,{"derivedFrom":[subQ0,sQuery(id+"F0.wireOp",EDGE,"E80")]}),-1.0]])],"derivedFrom":subQ0})])]});}
            var Q41;
            Q41=makeQuery(id+"F1.opRevolve","SWEPT_FACE",FACE,{"disambiguationData":[OSD([sQuery(id+"F0.wireOp",EDGE,"E83")])]});
            var Q42;
            {var subQ0=sQuery(id+"F0.wireOp",EDGE,"E20");Q42=makeQuery(id+"F1.opRevolve","SWEPT_FACE",FACE,{"disambiguationData":[OSD([subQ0]),TDD([makeQuery(id+"F0.imprint","IMPRINT",EDGE,{"disambiguationData":[TD([[makeQuery(id+"F0.imprint","INTERSECT",VERTEX,{"derivedFrom":[subQ0,sQuery(id+"F0.wireOp",EDGE,"E84")]}),-1.0]])],"derivedFrom":subQ0})])]});}
            var Q43;
            Q43=makeQuery(id+"F1.opRevolve","SWEPT_FACE",FACE,{"disambiguationData":[OSD([sQuery(id+"F0.wireOp",EDGE,"E86")])]});
            var Q44;
            {var subQ0=sQuery(id+"F0.wireOp",EDGE,"E20");Q44=makeQuery(id+"F1.opRevolve","SWEPT_FACE",FACE,{"disambiguationData":[OSD([subQ0]),TDD([makeQuery(id+"F0.imprint","IMPRINT",EDGE,{"disambiguationData":[TD([[makeQuery(id+"F0.imprint","INTERSECT",VERTEX,{"derivedFrom":[subQ0,sQuery(id+"F0.wireOp",EDGE,"E87")]}),-1.0]])],"derivedFrom":subQ0})])]});}
            var Q45;
            Q45=makeQuery(id+"F1.opRevolve","SWEPT_FACE",FACE,{"disambiguationData":[OSD([sQuery(id+"F0.wireOp",EDGE,"E89")])]});
            var Q46;
            {var subQ0=sQuery(id+"F0.wireOp",EDGE,"E20");Q46=makeQuery(id+"F1.opRevolve","SWEPT_FACE",FACE,{"disambiguationData":[OSD([subQ0]),TDD([makeQuery(id+"F0.imprint","IMPRINT",EDGE,{"disambiguationData":[TD([[makeQuery(id+"F0.imprint","INTERSECT",VERTEX,{"derivedFrom":[subQ0,sQuery(id+"F0.wireOp",EDGE,"E90")]}),-1.0]])],"derivedFrom":subQ0})])]});}
            var Q47;
            Q47=makeQuery(id+"F1.opRevolve","SWEPT_FACE",FACE,{"disambiguationData":[OSD([sQuery(id+"F0.wireOp",EDGE,"E92")])]});
            var Q48;
            {var subQ0=sQuery(id+"F0.wireOp",EDGE,"E20");Q48=makeQuery(id+"F1.opRevolve","SWEPT_FACE",FACE,{"disambiguationData":[OSD([subQ0]),TDD([makeQuery(id+"F0.imprint","IMPRINT",EDGE,{"disambiguationData":[TD([[makeQuery(id+"F0.imprint","INTERSECT",VERTEX,{"derivedFrom":[subQ0,sQuery(id+"F0.wireOp",EDGE,"E93")]}),-1.0]])],"derivedFrom":subQ0})])]});}
            var Q49;
            Q49=makeQuery(id+"F1.opRevolve","SWEPT_FACE",FACE,{"disambiguationData":[OSD([sQuery(id+"F0.wireOp",EDGE,"E95")])]});
            var Q50;
            {var subQ0=sQuery(id+"F0.wireOp",EDGE,"E20");Q50=makeQuery(id+"F1.opRevolve","SWEPT_FACE",FACE,{"disambiguationData":[OSD([subQ0]),TDD([makeQuery(id+"F0.imprint","IMPRINT",EDGE,{"disambiguationData":[TD([[makeQuery(id+"F0.imprint","INTERSECT",VERTEX,{"derivedFrom":[subQ0,sQuery(id+"F0.wireOp",EDGE,"E96")]}),-1.0]])],"derivedFrom":subQ0})])]});}
            var Q51;
            Q51=makeQuery(id+"F1.opRevolve","SWEPT_FACE",FACE,{"disambiguationData":[OSD([sQuery(id+"F0.wireOp",EDGE,"E98")])]});
            var Q52;
            {var subQ0=sQuery(id+"F0.wireOp",EDGE,"E20");Q52=makeQuery(id+"F1.opRevolve","SWEPT_FACE",FACE,{"disambiguationData":[OSD([subQ0]),TDD([makeQuery(id+"F0.imprint","IMPRINT",EDGE,{"disambiguationData":[TD([[makeQuery(id+"F0.imprint","INTERSECT",VERTEX,{"derivedFrom":[subQ0,sQuery(id+"F0.wireOp",EDGE,"E99")]}),-1.0]])],"derivedFrom":subQ0})])]});}
            var Q53;
            Q53=makeQuery(id+"F1.opRevolve","SWEPT_FACE",FACE,{"disambiguationData":[OSD([sQuery(id+"F0.wireOp",EDGE,"E101")])]});
            var Q54;
            {var subQ0=sQuery(id+"F0.wireOp",EDGE,"E20");Q54=makeQuery(id+"F1.opRevolve","SWEPT_FACE",FACE,{"disambiguationData":[OSD([subQ0]),TDD([makeQuery(id+"F0.imprint","IMPRINT",EDGE,{"disambiguationData":[TD([[makeQuery(id+"F0.imprint","INTERSECT",VERTEX,{"derivedFrom":[subQ0,sQuery(id+"F0.wireOp",EDGE,"E102")]}),-1.0]])],"derivedFrom":subQ0})])]});}
            var Q55;
            Q55=makeQuery(id+"F1.opRevolve","SWEPT_FACE",FACE,{"disambiguationData":[OSD([sQuery(id+"F0.wireOp",EDGE,"E104")])]});
            var Q56;
            {var subQ0=sQuery(id+"F0.wireOp",EDGE,"E20");Q56=makeQuery(id+"F1.opRevolve","SWEPT_FACE",FACE,{"disambiguationData":[OSD([subQ0]),TDD([makeQuery(id+"F0.imprint","IMPRINT",EDGE,{"disambiguationData":[TD([[makeQuery(id+"F0.imprint","INTERSECT",VERTEX,{"derivedFrom":[subQ0,sQuery(id+"F0.wireOp",EDGE,"E105")]}),-1.0]])],"derivedFrom":subQ0})])]});}
            var Q57;
            {var subQ0=sQuery(id+"F0.wireOp",EDGE,"E20");Q57=makeQuery(id+"F1.opRevolve","SWEPT_FACE",FACE,{"disambiguationData":[OSD([subQ0]),TDD([makeQuery(id+"F0.imprint","IMPRINT",EDGE,{"disambiguationData":[TD([[makeQuery(id+"F0.imprint","INTERSECT",VERTEX,{"derivedFrom":[subQ0,sQuery(id+"F0.wireOp",EDGE,"E108")]}),-1.0]])],"derivedFrom":subQ0})])]});}
            var Q58;
            Q58=makeQuery(id+"F1.opRevolve","SWEPT_FACE",FACE,{"disambiguationData":[OSD([sQuery(id+"F0.wireOp",EDGE,"E110")])]});
            var Q59;
            Q59=makeQuery(id+"F1.opRevolve","SWEPT_FACE",FACE,{"disambiguationData":[OSD([sQuery(id+"F0.wireOp",EDGE,"E113")])]});
            var Q60;
            Q60=makeQuery(id+"F1.opRevolve","SWEPT_FACE",FACE,{"disambiguationData":[OSD([sQuery(id+"F0.wireOp",EDGE,"E107")])]});
            var Q61;
            {var subQ0=sQuery(id+"F0.wireOp",EDGE,"E20");Q61=makeQuery(id+"F1.opRevolve","SWEPT_FACE",FACE,{"disambiguationData":[OSD([subQ0]),TDD([makeQuery(id+"F0.imprint","IMPRINT",EDGE,{"disambiguationData":[TD([[makeQuery(id+"F0.imprint","INTERSECT",VERTEX,{"derivedFrom":[subQ0,sQuery(id+"F0.wireOp",EDGE,"E114")]}),-1.0]])],"derivedFrom":subQ0})])]});}
            var Q62;
            Q62=makeQuery(id+"F1.opRevolve","SWEPT_FACE",FACE,{"disambiguationData":[OSD([sQuery(id+"F0.wireOp",EDGE,"E116")])]});
            var Q63;
            {var subQ0=sQuery(id+"F0.wireOp",EDGE,"E20");Q63=makeQuery(id+"F1.opRevolve","SWEPT_FACE",FACE,{"disambiguationData":[OSD([subQ0]),TDD([makeQuery(id+"F0.imprint","IMPRINT",EDGE,{"disambiguationData":[TD([[makeQuery(id+"F0.imprint","INTERSECT",VERTEX,{"derivedFrom":[subQ0,sQuery(id+"F0.wireOp",EDGE,"E117")]}),-1.0]])],"derivedFrom":subQ0})])]});}
            var Q64;
            Q64=makeQuery(id+"F1.opRevolve","SWEPT_FACE",FACE,{"disambiguationData":[OSD([sQuery(id+"F0.wireOp",EDGE,"E119")])]});
            var Q65;
            {var subQ0=sQuery(id+"F0.wireOp",EDGE,"E20");Q65=makeQuery(id+"F1.opRevolve","SWEPT_FACE",FACE,{"disambiguationData":[OSD([subQ0]),TDD([makeQuery(id+"F0.imprint","IMPRINT",EDGE,{"disambiguationData":[TD([[makeQuery(id+"F0.imprint","INTERSECT",VERTEX,{"derivedFrom":[subQ0,sQuery(id+"F0.wireOp",EDGE,"E120")]}),-1.0]])],"derivedFrom":subQ0})])]});}
            var Q66;
            Q66=makeQuery(id+"F1.opRevolve","SWEPT_FACE",FACE,{"disambiguationData":[OSD([sQuery(id+"F0.wireOp",EDGE,"E122")])]});
            var Q67;
            {var subQ0=sQuery(id+"F0.wireOp",EDGE,"E20");Q67=makeQuery(id+"F1.opRevolve","SWEPT_FACE",FACE,{"disambiguationData":[OSD([subQ0]),TDD([makeQuery(id+"F0.imprint","IMPRINT",EDGE,{"disambiguationData":[TD([[makeQuery(id+"F0.imprint","INTERSECT",VERTEX,{"derivedFrom":[subQ0,sQuery(id+"F0.wireOp",EDGE,"E123")]}),-1.0]])],"derivedFrom":subQ0})])]});}
            var Q68;
            Q68=makeQuery(id+"F1.opRevolve","SWEPT_FACE",FACE,{"disambiguationData":[OSD([sQuery(id+"F0.wireOp",EDGE,"E125")])]});
            var Q69;
            {var subQ0=sQuery(id+"F0.wireOp",EDGE,"E20");Q69=makeQuery(id+"F1.opRevolve","SWEPT_FACE",FACE,{"disambiguationData":[OSD([subQ0]),TDD([makeQuery(id+"F0.imprint","IMPRINT",EDGE,{"disambiguationData":[TD([[makeQuery(id+"F0.imprint","INTERSECT",VERTEX,{"derivedFrom":[subQ0,sQuery(id+"F0.wireOp",EDGE,"E126")]}),-1.0]])],"derivedFrom":subQ0})])]});}
            var Q70;
            Q70=makeQuery(id+"F1.opRevolve","SWEPT_FACE",FACE,{"disambiguationData":[OSD([sQuery(id+"F0.wireOp",EDGE,"E128")])]});
            var Q71;
            {var subQ0=sQuery(id+"F0.wireOp",EDGE,"E20");Q71=makeQuery(id+"F1.opRevolve","SWEPT_FACE",FACE,{"disambiguationData":[OSD([subQ0]),TDD([makeQuery(id+"F0.imprint","IMPRINT",EDGE,{"disambiguationData":[TD([[makeQuery(id+"F0.imprint","INTERSECT",VERTEX,{"derivedFrom":[subQ0,sQuery(id+"F0.wireOp",EDGE,"E129")]}),-1.0]])],"derivedFrom":subQ0})])]});}
            var Q72;
            Q72=makeQuery(id+"F1.opRevolve","SWEPT_FACE",FACE,{"disambiguationData":[OSD([sQuery(id+"F0.wireOp",EDGE,"E131")])]});
            var Q73;
            {var subQ0=sQuery(id+"F0.wireOp",EDGE,"E20");Q73=makeQuery(id+"F1.opRevolve","SWEPT_FACE",FACE,{"disambiguationData":[OSD([subQ0]),TDD([makeQuery(id+"F0.imprint","IMPRINT",EDGE,{"disambiguationData":[TD([[makeQuery(id+"F0.imprint","INTERSECT",VERTEX,{"derivedFrom":[subQ0,sQuery(id+"F0.wireOp",EDGE,"E132")]}),-1.0]])],"derivedFrom":subQ0})])]});}
            var Q74;
            Q74=makeQuery(id+"F1.opRevolve","SWEPT_FACE",FACE,{"disambiguationData":[OSD([sQuery(id+"F0.wireOp",EDGE,"E134")])]});
            var Q75;
            {var subQ0=sQuery(id+"F0.wireOp",EDGE,"E20");Q75=makeQuery(id+"F1.opRevolve","SWEPT_FACE",FACE,{"disambiguationData":[OSD([subQ0]),TDD([makeQuery(id+"F0.imprint","IMPRINT",EDGE,{"disambiguationData":[TD([[makeQuery(id+"F0.imprint","INTERSECT",VERTEX,{"derivedFrom":[subQ0,sQuery(id+"F0.wireOp",EDGE,"E135")]}),-1.0]])],"derivedFrom":subQ0})])]});}
            var Q76;
            Q76=makeQuery(id+"F1.opRevolve","SWEPT_FACE",FACE,{"disambiguationData":[OSD([sQuery(id+"F0.wireOp",EDGE,"E137")])]});
            var Q77;
            {var subQ0=sQuery(id+"F0.wireOp",EDGE,"E20");Q77=makeQuery(id+"F1.opRevolve","SWEPT_FACE",FACE,{"disambiguationData":[OSD([subQ0]),TDD([makeQuery(id+"F0.imprint","IMPRINT",EDGE,{"disambiguationData":[TD([[makeQuery(id+"F0.imprint","INTERSECT",VERTEX,{"derivedFrom":[subQ0,sQuery(id+"F0.wireOp",EDGE,"E138")]}),-1.0]])],"derivedFrom":subQ0})])]});}
            var Q78;
            Q78=makeQuery(id+"F1.opRevolve","SWEPT_FACE",FACE,{"disambiguationData":[OSD([sQuery(id+"F0.wireOp",EDGE,"E140")])]});
            var Q79;
            {var subQ0=sQuery(id+"F0.wireOp",EDGE,"E20");Q79=makeQuery(id+"F1.opRevolve","SWEPT_FACE",FACE,{"disambiguationData":[OSD([subQ0]),TDD([makeQuery(id+"F0.imprint","IMPRINT",EDGE,{"disambiguationData":[TD([[makeQuery(id+"F0.imprint","INTERSECT",VERTEX,{"derivedFrom":[subQ0,sQuery(id+"F0.wireOp",EDGE,"E141")]}),-1.0]])],"derivedFrom":subQ0})])]});}
            var Q80;
            Q80=makeQuery(id+"F1.opRevolve","SWEPT_FACE",FACE,{"disambiguationData":[OSD([sQuery(id+"F0.wireOp",EDGE,"E143")])]});
            var Q81;
            {var subQ0=sQuery(id+"F0.wireOp",EDGE,"E20");Q81=makeQuery(id+"F1.opRevolve","SWEPT_FACE",FACE,{"disambiguationData":[OSD([subQ0]),TDD([makeQuery(id+"F0.imprint","IMPRINT",EDGE,{"disambiguationData":[TD([[makeQuery(id+"F0.imprint","INTERSECT",VERTEX,{"derivedFrom":[subQ0,sQuery(id+"F0.wireOp",EDGE,"E144")]}),-1.0]])],"derivedFrom":subQ0})])]});}
            var Q82;
            Q82=makeQuery(id+"F1.opRevolve","SWEPT_FACE",FACE,{"disambiguationData":[OSD([sQuery(id+"F0.wireOp",EDGE,"E146")])]});
            var Q83;
            {var subQ0=sQuery(id+"F0.wireOp",EDGE,"E20");Q83=makeQuery(id+"F1.opRevolve","SWEPT_FACE",FACE,{"disambiguationData":[OSD([subQ0]),TDD([makeQuery(id+"F0.imprint","IMPRINT",EDGE,{"disambiguationData":[TD([[makeQuery(id+"F0.imprint","INTERSECT",VERTEX,{"derivedFrom":[subQ0,sQuery(id+"F0.wireOp",EDGE,"E147")]}),-1.0]])],"derivedFrom":subQ0})])]});}
            var Q84;
            Q84=makeQuery(id+"F1.opRevolve","SWEPT_FACE",FACE,{"disambiguationData":[OSD([sQuery(id+"F0.wireOp",EDGE,"E149")])]});
            var Q85;
            {var subQ0=sQuery(id+"F0.wireOp",EDGE,"E20");Q85=makeQuery(id+"F1.opRevolve","SWEPT_FACE",FACE,{"disambiguationData":[OSD([subQ0]),TDD([makeQuery(id+"F0.imprint","IMPRINT",EDGE,{"disambiguationData":[TD([[makeQuery(id+"F0.imprint","INTERSECT",VERTEX,{"derivedFrom":[subQ0,sQuery(id+"F0.wireOp",EDGE,"E150")]}),-1.0]])],"derivedFrom":subQ0})])]});}
            var Q86;
            Q86=makeQuery(id+"F1.opRevolve","SWEPT_FACE",FACE,{"disambiguationData":[OSD([sQuery(id+"F0.wireOp",EDGE,"E152")])]});
            var Q87;
            Q87=makeQuery(id+"F1.opRevolve","SWEPT_EDGE",EDGE,{"disambiguationData":[OSD([sQuery(id+"F0.wireOp",EDGE,"E20"),sQuery(id+"F0.wireOp",EDGE,"E153")])]});
            var Q88;
            {var subQ0=sQuery(id+"F0.wireOp",EDGE,"E20");Q88=makeQuery(id+"F1.opRevolve","SWEPT_FACE",FACE,{"disambiguationData":[OSD([subQ0]),TDD([makeQuery(id+"F0.imprint","IMPRINT",EDGE,{"disambiguationData":[TD([[makeQuery(id+"F0.imprint","INTERSECT",VERTEX,{"derivedFrom":[subQ0,sQuery(id+"F0.wireOp",EDGE,"E111")]}),-1.0]])],"derivedFrom":subQ0})])]});}
            fillet(context, id + "F3", {"entities" : qUnion([Q0, Q1, Q2, Q3, Q4, Q5, Q6, Q7, Q8, Q9, Q10, Q11, Q12, Q13, Q14, Q15, Q16, Q17, Q18, Q19, Q20, Q21, Q22, Q23, Q24, Q25, Q26, Q27, Q28, Q29, Q30, Q31, Q32, Q33, Q34, Q35, Q36, Q37, Q38, Q39, Q40, Q41, Q42, Q43, Q44, Q45, Q46, Q47, Q48, Q49, Q50, Q51, Q52, Q53, Q54, Q55, Q56, Q57, Q58, Q59, Q60, Q61, Q62, Q63, Q64, Q65, Q66, Q67, Q68, Q69, Q70, Q71, Q72, Q73, Q74, Q75, Q76, Q77, Q78, Q79, Q80, Q81, Q82, Q83, Q84, Q85, Q86, Q87, Q88]), "radius" : 1 * mm, "tangentPropagation" : true, "allowEdgeOverflow" : false});
        }
        {
            var Q0;
            Q0=makeQuery(id+"F1.opRevolve","SWEPT_EDGE",EDGE,{"disambiguationData":[OSD([sQuery(id+"F0.wireOp",EDGE,"E20"),sQuery(id+"F0.wireOp",EDGE,"E154")])]});
            fillet(context, id + "F4", {"entities" : qUnion([Q0]), "radius" : 3 * mm, "tangentPropagation" : true, "allowEdgeOverflow" : false});
        }
        {
            var Q0;
            Q0=makeQuery(id+"F1.opRevolve","SWEPT_EDGE",EDGE,{"disambiguationData":[OSD([sQuery(id+"F0.wireOp",EDGE,"E154"),sQuery(id+"F0.wireOp",EDGE,"E155")])]});
            var Q1;
            Q1=makeQuery(id+"F1.opRevolve","SWEPT_EDGE",EDGE,{"disambiguationData":[OSD([sQuery(id+"F0.wireOp",EDGE,"E155"),sQuery(id+"F0.wireOp",EDGE,"E156"),sQuery(id+"F0.wireOp",EDGE,"E157")])]});
            fillet(context, id + "F5", {"entities" : qUnion([Q0, Q1]), "radius" : 0.5 * mm, "tangentPropagation" : true, "allowEdgeOverflow" : false});
        }
        {
            var Q0;
            Q0=makeQuery(id+"F1.opRevolve","SWEPT_EDGE",EDGE,{"disambiguationData":[OSD([sQuery(id+"F0.wireOp",EDGE,"E157"),sQuery(id+"F0.wireOp",EDGE,"E158")])]});
            fillet(context, id + "F6", {"entities" : qUnion([Q0]), "radius" : 0.25 * mm, "tangentPropagation" : true, "allowEdgeOverflow" : false});
        }
        {
            var Q0;
            Q0=makeQuery(id+"F1.opRevolve","SWEPT_FACE",FACE,{"disambiguationData":[OSD([sQuery(id+"F0.wireOp",EDGE,"E159"),sQuery(id+"F0.wireOp",EDGE,"E160")])]});
            var sketch = newSketch(context, id + "F7", { "sketchPlane" : qUnion([Q0])});
            skCircle(sketch, "E161", {"center": v(0, 0) * mm, "radius": 3.85 * mm});
            skCircle(sketch, "E162.cCircle", {"center": v(0, 0) * mm, "radius": 17.7 * mm, "construction": true});
            skLineSegment(sketch, "E162.0", {"start": v(0, 17.7) * mm, "end": v(15.33, 8.85) * mm});
            skLineSegment(sketch, "E162.1", {"start": v(15.33, 8.85) * mm, "end": v(15.33, -8.85) * mm});
            skLineSegment(sketch, "E162.2", {"start": v(15.33, -8.85) * mm, "end": v(0, -17.7) * mm});
            skLineSegment(sketch, "E162.3", {"start": v(0, -17.7) * mm, "end": v(-15.33, -8.85) * mm});
            skLineSegment(sketch, "E162.4", {"start": v(-15.33, -8.85) * mm, "end": v(-15.33, 8.85) * mm});
            skLineSegment(sketch, "E162.5", {"start": v(-15.33, 8.85) * mm, "end": v(0, 17.7) * mm});
            skSolve(sketch);
        }
        {
            var Q0;
            Q0 = qSketchRegion(id + "F7", true);
            extrude(context, id + "F8", {"entities" : qUnion([Q0]), "operationType" : NewBodyOperationType.ADD, "depth" : 9 * mm});
        }
        {
            var Q0;
            Q0=qCreatedBy(makeId("Front.planeOp"),FACE);
            var sketch = newSketch(context, id + "F9", { "sketchPlane" : qUnion([Q0])});
            skLineSegment(sketch, "E163", {"start": v(-312.5, 17.7) * mm, "end": v(-312.5, 15.7) * mm});
            skPoint(sketch, "E164", {"position": v(-312.5, 17.7) * mm});
            skLineSegment(sketch, "E165", {"start": v(-312.5, 15.7) * mm, "end": v(-310.7, 17.7) * mm});
            skLineSegment(sketch, "E166", {"start": v(-310.7, 17.7) * mm, "end": v(-312.5, 17.7) * mm});
            skSolve(sketch);
        }
        {
            var Q0;
            Q0 = qSketchRegion(id + "F9", true);
            var Q1;
            Q1=sQuery(id+"F0.wireOp",EDGE,"E0");
            revolve(context, id + "F10", {"operationType" : NewBodyOperationType.REMOVE, "entities" : qUnion([Q0]), "axis" : qUnion([Q1]), "revolveType" : RevolveType.FULL, "oppositeDirection" : true});
        }
    });
